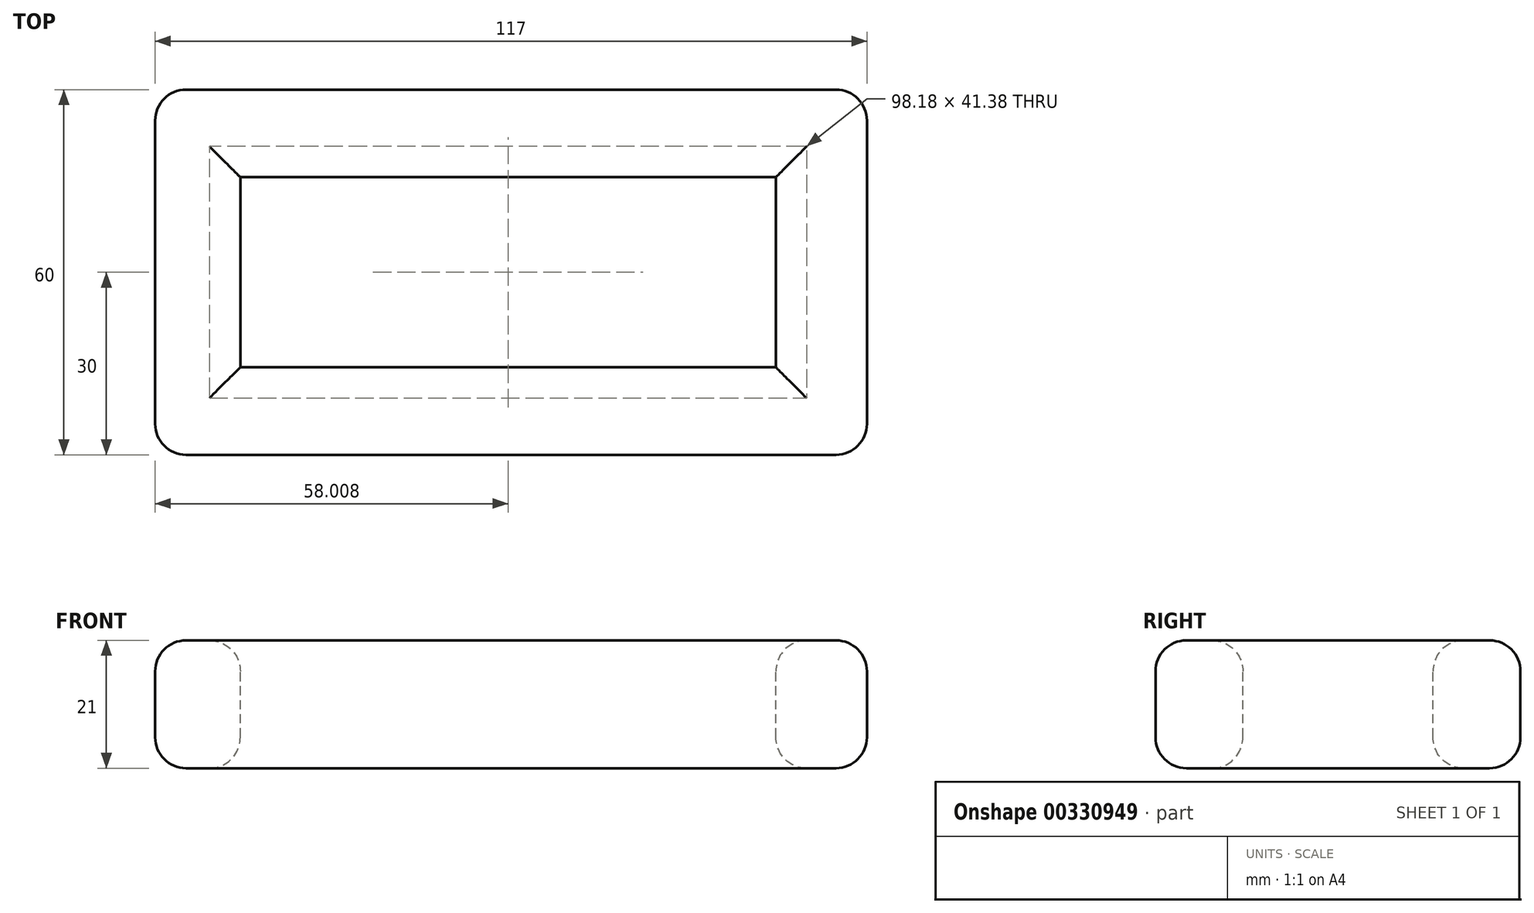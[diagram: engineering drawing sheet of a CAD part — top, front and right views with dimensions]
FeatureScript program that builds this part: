
annotation { "Feature Type Name" : "Feature", "Feature Type Description" : "" }
export const myFeature = defineFeature(function(context is Context, id is Id, definition is map)
    precondition{}
    {
        {
            var Q0;
            Q0=qCreatedBy(makeId("Top.planeOp"),FACE);
            var sketch = newSketch(context, id + "F0", { "sketchPlane" : qUnion([Q0])});
            skLineSegment(sketch, "E0.bottom", {"start": v(-56.82, 74.45) * mm, "end": v(60.18, 74.45) * mm});
            skLineSegment(sketch, "E0.top", {"start": v(-56.82, 14.45) * mm, "end": v(60.18, 14.45) * mm});
            skLineSegment(sketch, "E0.left", {"start": v(-56.82, 74.45) * mm, "end": v(-56.82, 14.45) * mm});
            skLineSegment(sketch, "E0.right", {"start": v(60.18, 74.45) * mm, "end": v(60.18, 14.45) * mm});
            skLineSegment(sketch, "E1.bottom", {"start": v(-42.82, 60.06) * mm, "end": v(45.2, 60.06) * mm});
            skLineSegment(sketch, "E1.top", {"start": v(-42.82, 28.84) * mm, "end": v(45.2, 28.84) * mm});
            skLineSegment(sketch, "E1.left", {"start": v(-42.82, 60.06) * mm, "end": v(-42.82, 28.84) * mm});
            skLineSegment(sketch, "E1.right", {"start": v(45.2, 60.06) * mm, "end": v(45.2, 28.84) * mm});
            skSolve(sketch);
        }
        {
            var Q0;
            Q0=makeQuery(id+"F0.imprint","IMPRINT",FACE,{"disambiguationData":[TD([[makeQuery(id+"F0.imprint","IMPRINT",EDGE,{"derivedFrom":sQuery(id+"F0.wireOp",EDGE,"E0.bottom")}),-1.0]])]});
            extrude(context, id + "F1", {"entities" : qUnion([Q0]), "oppositeDirection" : true, "depth" : 21 * mm});
        }
        {
            var Q0;
            Q0=makeQuery(id+"F1.opExtrude","CAP_EDGE",EDGE,{"disambiguationData":[OSD([sQuery(id+"F0.wireOp",EDGE,"E0.left")])],"isStart":true});
            var Q1;
            Q1=makeQuery(id+"F1.opExtrude","CAP_EDGE",EDGE,{"disambiguationData":[OSD([sQuery(id+"F0.wireOp",EDGE,"E0.top")])],"isStart":true});
            var Q2;
            Q2=makeQuery(id+"F1.opExtrude","CAP_EDGE",EDGE,{"disambiguationData":[OSD([sQuery(id+"F0.wireOp",EDGE,"E0.right")])],"isStart":true});
            var Q3;
            Q3=makeQuery(id+"F1.opExtrude","CAP_EDGE",EDGE,{"disambiguationData":[OSD([sQuery(id+"F0.wireOp",EDGE,"E0.bottom")])],"isStart":true});
            var Q4;
            Q4=makeQuery(id+"F1.opExtrude","CAP_EDGE",EDGE,{"disambiguationData":[OSD([sQuery(id+"F0.wireOp",EDGE,"E0.top")])],"isStart":false});
            var Q5;
            Q5=makeQuery(id+"F1.opExtrude","CAP_EDGE",EDGE,{"disambiguationData":[OSD([sQuery(id+"F0.wireOp",EDGE,"E0.right")])],"isStart":false});
            var Q6;
            Q6=makeQuery(id+"F1.opExtrude","CAP_EDGE",EDGE,{"disambiguationData":[OSD([sQuery(id+"F0.wireOp",EDGE,"E0.bottom")])],"isStart":false});
            var Q7;
            Q7=makeQuery(id+"F1.opExtrude","CAP_EDGE",EDGE,{"disambiguationData":[OSD([sQuery(id+"F0.wireOp",EDGE,"E0.left")])],"isStart":false});
            var Q8;
            Q8=makeQuery(id+"F1.opExtrude","SWEPT_EDGE",EDGE,{"disambiguationData":[OSD([sQuery(id+"F0.wireOp",EDGE,"E0.top"),sQuery(id+"F0.wireOp",EDGE,"E0.left")])]});
            var Q9;
            Q9=makeQuery(id+"F1.opExtrude","SWEPT_EDGE",EDGE,{"disambiguationData":[OSD([sQuery(id+"F0.wireOp",EDGE,"E0.bottom"),sQuery(id+"F0.wireOp",EDGE,"E0.left")])]});
            var Q10;
            Q10=makeQuery(id+"F1.opExtrude","SWEPT_EDGE",EDGE,{"disambiguationData":[OSD([sQuery(id+"F0.wireOp",EDGE,"E0.top"),sQuery(id+"F0.wireOp",EDGE,"E0.right")])]});
            var Q11;
            Q11=makeQuery(id+"F1.opExtrude","SWEPT_FACE",FACE,{"disambiguationData":[OSD([sQuery(id+"F0.wireOp",EDGE,"E0.right")])]});
            var Q12;
            Q12=makeQuery(id+"F1.opExtrude","CAP_EDGE",EDGE,{"disambiguationData":[OSD([sQuery(id+"F0.wireOp",EDGE,"E1.right")])],"isStart":false});
            var Q13;
            Q13=makeQuery(id+"F1.opExtrude","CAP_EDGE",EDGE,{"disambiguationData":[OSD([sQuery(id+"F0.wireOp",EDGE,"E1.bottom")])],"isStart":false});
            var Q14;
            Q14=makeQuery(id+"F1.opExtrude","CAP_EDGE",EDGE,{"disambiguationData":[OSD([sQuery(id+"F0.wireOp",EDGE,"E1.left")])],"isStart":false});
            var Q15;
            Q15=makeQuery(id+"F1.opExtrude","CAP_EDGE",EDGE,{"disambiguationData":[OSD([sQuery(id+"F0.wireOp",EDGE,"E1.top")])],"isStart":false});
            var Q16;
            Q16=makeQuery(id+"F1.opExtrude","CAP_EDGE",EDGE,{"disambiguationData":[OSD([sQuery(id+"F0.wireOp",EDGE,"E1.top")])],"isStart":true});
            var Q17;
            Q17=makeQuery(id+"F1.opExtrude","CAP_EDGE",EDGE,{"disambiguationData":[OSD([sQuery(id+"F0.wireOp",EDGE,"E1.left")])],"isStart":true});
            var Q18;
            Q18=makeQuery(id+"F1.opExtrude","CAP_EDGE",EDGE,{"disambiguationData":[OSD([sQuery(id+"F0.wireOp",EDGE,"E1.right")])],"isStart":true});
            var Q19;
            Q19=makeQuery(id+"F1.opExtrude","CAP_EDGE",EDGE,{"disambiguationData":[OSD([sQuery(id+"F0.wireOp",EDGE,"E1.bottom")])],"isStart":true});
            fillet(context, id + "F2", {"entities" : qUnion([Q0, Q1, Q2, Q3, Q4, Q5, Q6, Q7, Q8, Q9, Q10, Q11, Q12, Q13, Q14, Q15, Q16, Q17, Q18, Q19]), "radius" : 5.08 * mm, "tangentPropagation" : true, "allowEdgeOverflow" : false});
        }
    });
